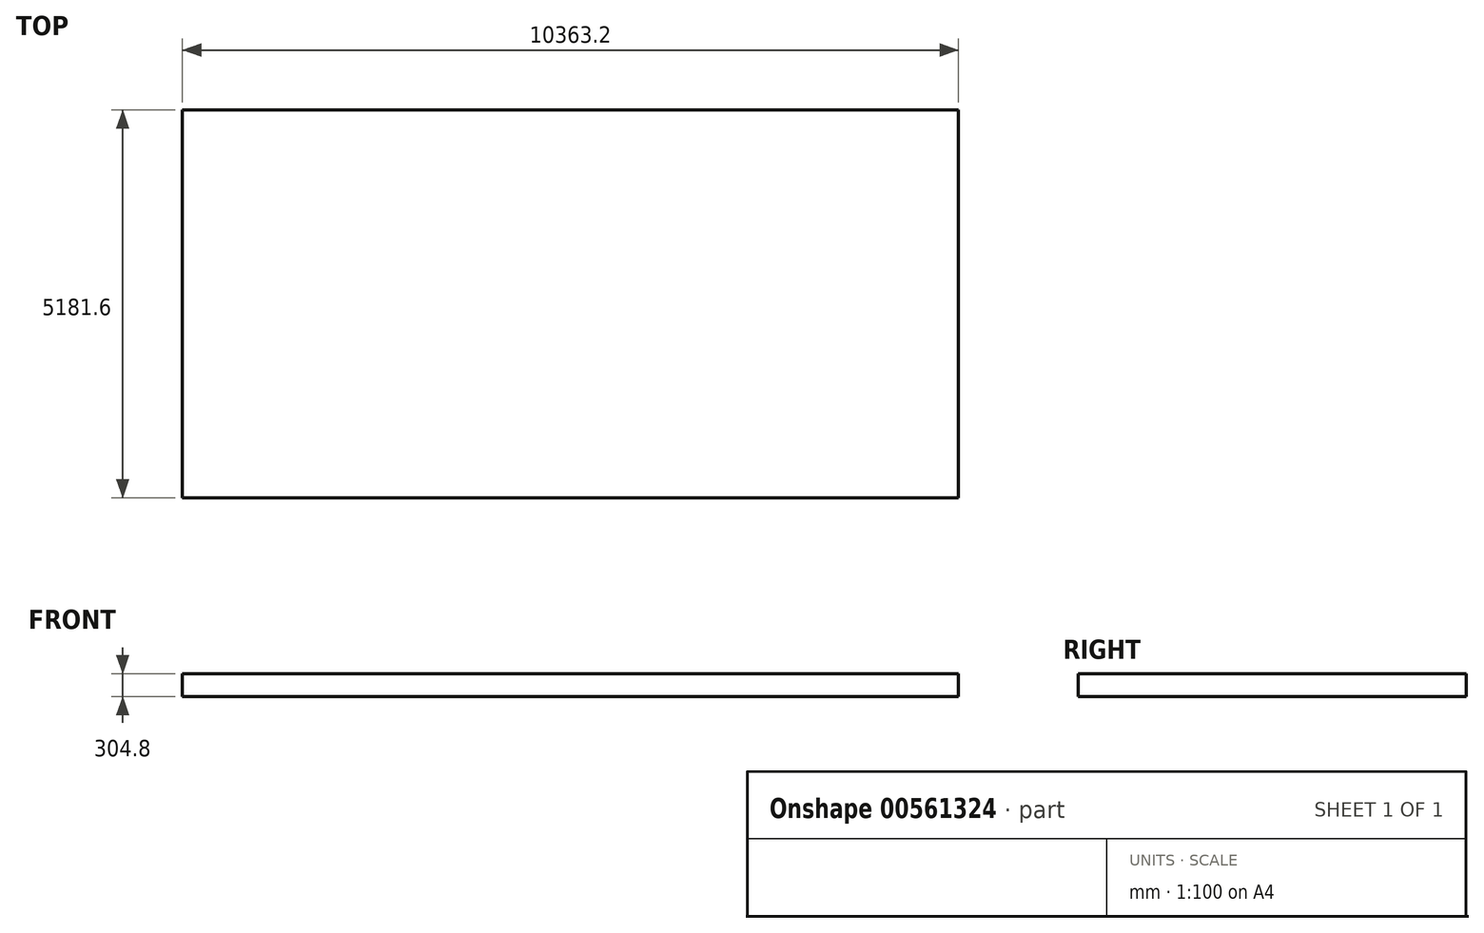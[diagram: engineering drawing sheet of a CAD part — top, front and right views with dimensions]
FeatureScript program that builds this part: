
annotation { "Feature Type Name" : "Feature", "Feature Type Description" : "" }
export const myFeature = defineFeature(function(context is Context, id is Id, definition is map)
    precondition{}
    {
        {
            var Q0;
            Q0=qCreatedBy(makeId("Top.planeOp"),FACE);
            var sketch = newSketch(context, id + "F0", { "sketchPlane" : qUnion([Q0])});
            skLineSegment(sketch, "E0.bottom", {"start": v(-5177, 478.98) * mm, "end": v(5186.2, 478.98) * mm});
            skLineSegment(sketch, "E0.top", {"start": v(-5177, -4702.62) * mm, "end": v(5186.2, -4702.62) * mm});
            skLineSegment(sketch, "E0.left", {"start": v(-5177, 478.98) * mm, "end": v(-5177, -4702.62) * mm});
            skLineSegment(sketch, "E0.right", {"start": v(5186.2, 478.98) * mm, "end": v(5186.2, -4702.62) * mm});
            skSolve(sketch);
        }
        {
            var Q0;
            Q0 = qSketchRegion(id + "F0", true);
            extrude(context, id + "F1", {"entities" : qUnion([Q0]), "depth" : 304.8 * mm, "offsetDistance" : 30.48 * mm});
        }
    });
